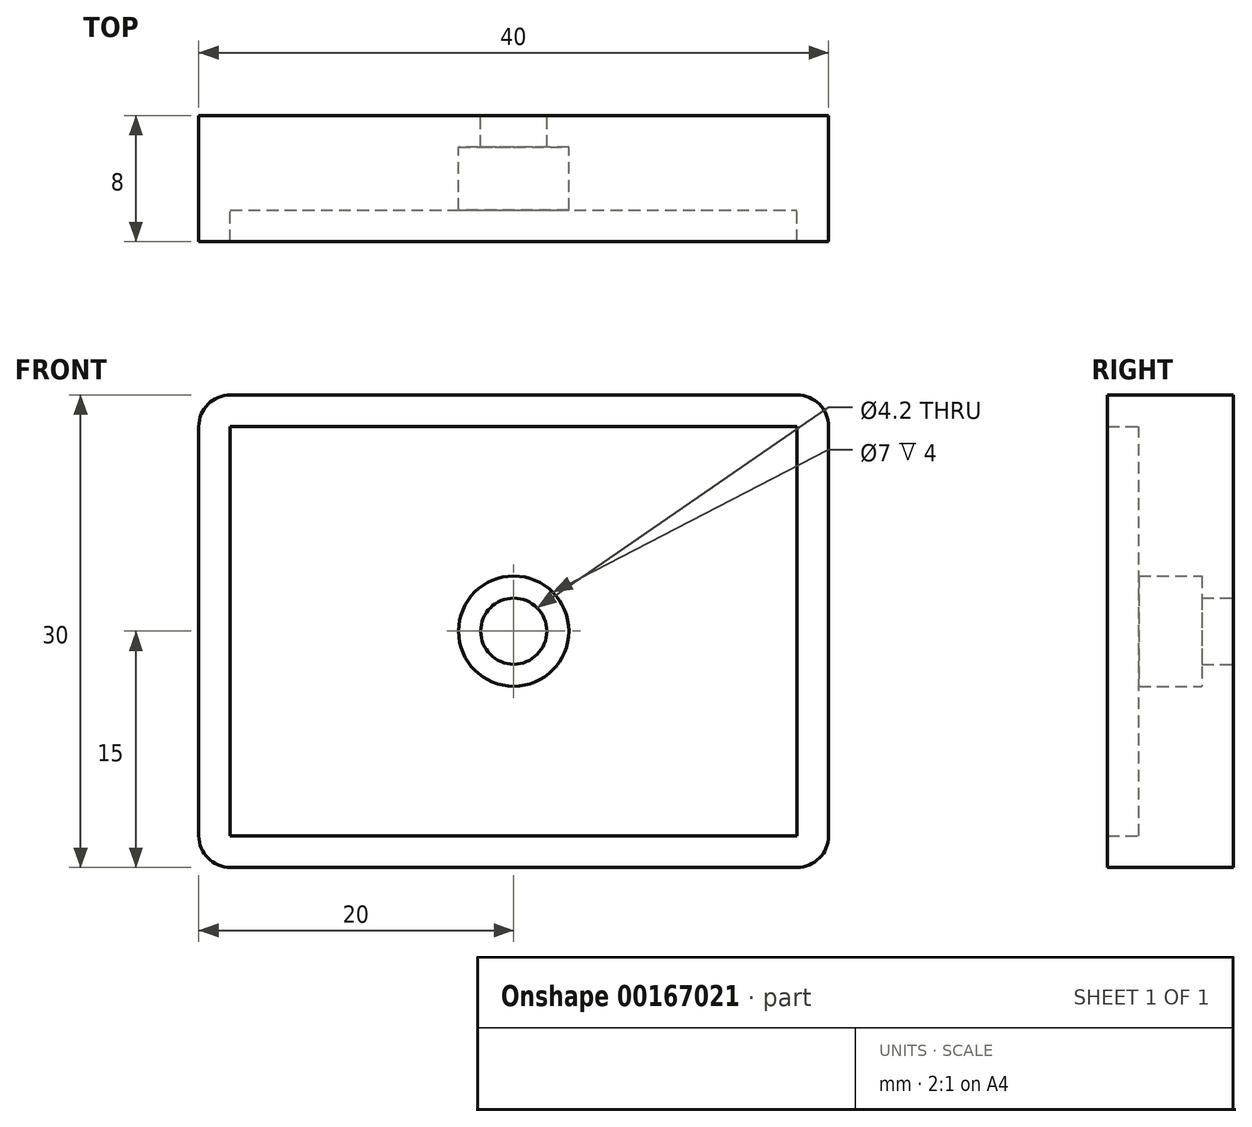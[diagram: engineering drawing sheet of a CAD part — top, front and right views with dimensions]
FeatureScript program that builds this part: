
annotation { "Feature Type Name" : "Feature", "Feature Type Description" : "" }
export const myFeature = defineFeature(function(context is Context, id is Id, definition is map)
    precondition{}
    {
        {
            var Q0;
            Q0=qCreatedBy(makeId("Front.planeOp"),FACE);
            var sketch = newSketch(context, id + "F0", { "sketchPlane" : qUnion([Q0])});
            skLineSegment(sketch, "E0", {"start": v(0, 0) * mm, "end": v(-40, 0) * mm});
            skLineSegment(sketch, "E1", {"start": v(-40, 0) * mm, "end": v(-40, 30) * mm});
            skLineSegment(sketch, "E2", {"start": v(-40, 30) * mm, "end": v(0, 30) * mm});
            skLineSegment(sketch, "E3", {"start": v(0, 30) * mm, "end": v(0, 0) * mm});
            skLineSegment(sketch, "E4.0", {"start": v(-38, 28) * mm, "end": v(-2, 28) * mm});
            skLineSegment(sketch, "E4.1", {"start": v(-38, 2) * mm, "end": v(-38, 28) * mm});
            skLineSegment(sketch, "E4.2", {"start": v(-2, 2) * mm, "end": v(-38, 2) * mm});
            skLineSegment(sketch, "E4.3", {"start": v(-2, 28) * mm, "end": v(-2, 2) * mm});
            skLineSegment(sketch, "E5", {"start": v(-40, 15) * mm, "end": v(-20, 15) * mm});
            skSolve(sketch);
        }
        {
            var Q0;
            Q0 = qSketchRegion(id + "F0", true);
            var Q1;
            Q1=makeQuery(id+"F0.imprint","IMPRINT",FACE,{"disambiguationData":[TD([[makeQuery(id+"F0.imprint","IMPRINT",EDGE,{"derivedFrom":sQuery(id+"F0.wireOp",EDGE,"E4.0")}),-1.0]])]});
            extrude(context, id + "F1", {"entities" : qUnion([Q0, Q1]), "oppositeDirection" : true, "depth" : 6 * mm, "offsetDistance" : 25 * mm});
        }
        {
            var Q0;
            Q0=makeQuery(id+"F0.imprint","IMPRINT",FACE,{"disambiguationData":[TD([[makeQuery(id+"F0.imprint","IMPRINT",EDGE,{"derivedFrom":sQuery(id+"F0.wireOp",EDGE,"E0")}),-1.0]])]});
            extrude(context, id + "F2", {"entities" : qUnion([Q0]), "operationType" : NewBodyOperationType.ADD, "depth" : 2 * mm, "offsetDistance" : 25 * mm});
        }
        {
            var Q0;
            Q0=sQuery(id+"F0.wireOp",VERTEX,"E5.end");
            var Q1;
            Q1=makeQuery(id+"F1.opExtrude","SWEPT_BODY",BODY,{"disambiguationData":[OSD([sQuery(id+"F0.wireOp",EDGE,"E0"),sQuery(id+"F0.wireOp",EDGE,"E1"),sQuery(id+"F0.wireOp",EDGE,"E2"),sQuery(id+"F0.wireOp",EDGE,"E3")])]});
            hole(context, id + "F3", {"style" : HoleStyle.C_BORE, "endStyle" : HoleEndStyle.BLIND, "holeDiameter" : 4.2 * mm, "cBoreDiameter" : 7 * mm, "cBoreDepth" : 4 * mm, "majorDiameter" : 5 * mm, "holeDepth" : 15 * mm, "isTappedThrough" : true, "tappedDepth" : 12 * mm, "tapClearance" : 3, "locations" : qUnion([Q0]), "scope" : qUnion([Q1]), "startStyle" : HoleStartStyle.PART});
        }
        {
            var Q0;
            {var subQ0=sQuery(id+"F0.wireOp",EDGE,"E2");var subQ1=sQuery(id+"F0.wireOp",EDGE,"E1");Q0=makeQuery(id+"F2.boolean.opBoolean","MERGE",EDGE,{"derivedFrom":[makeQuery(id+"F1.opExtrude","SWEPT_EDGE",EDGE,{"disambiguationData":[OSD([subQ1,subQ0])]}),makeQuery(id+"F2.opExtrude","SWEPT_EDGE",EDGE,{"disambiguationData":[OSD([subQ1,subQ0])]})]});}
            var Q1;
            {var subQ0=sQuery(id+"F0.wireOp",EDGE,"E3");var subQ1=sQuery(id+"F0.wireOp",EDGE,"E2");Q1=makeQuery(id+"F2.boolean.opBoolean","MERGE",EDGE,{"derivedFrom":[makeQuery(id+"F1.opExtrude","SWEPT_EDGE",EDGE,{"disambiguationData":[OSD([subQ1,subQ0])]}),makeQuery(id+"F2.opExtrude","SWEPT_EDGE",EDGE,{"disambiguationData":[OSD([subQ1,subQ0])]})]});}
            var Q2;
            {var subQ0=sQuery(id+"F0.wireOp",EDGE,"E3");var subQ1=sQuery(id+"F0.wireOp",EDGE,"E0");Q2=makeQuery(id+"F2.boolean.opBoolean","MERGE",EDGE,{"derivedFrom":[makeQuery(id+"F1.opExtrude","SWEPT_EDGE",EDGE,{"disambiguationData":[OSD([subQ1,subQ0])]}),makeQuery(id+"F2.opExtrude","SWEPT_EDGE",EDGE,{"disambiguationData":[OSD([subQ1,subQ0])]})]});}
            var Q3;
            {var subQ0=sQuery(id+"F0.wireOp",EDGE,"E1");var subQ1=sQuery(id+"F0.wireOp",EDGE,"E0");Q3=makeQuery(id+"F2.boolean.opBoolean","MERGE",EDGE,{"derivedFrom":[makeQuery(id+"F1.opExtrude","SWEPT_EDGE",EDGE,{"disambiguationData":[OSD([subQ1,subQ0])]}),makeQuery(id+"F2.opExtrude","SWEPT_EDGE",EDGE,{"disambiguationData":[OSD([subQ1,subQ0])]})]});}
            fillet(context, id + "F4", {"entities" : qUnion([Q0, Q1, Q2, Q3]), "radius" : 2 * mm, "tangentPropagation" : true, "allowEdgeOverflow" : false});
        }
    });
